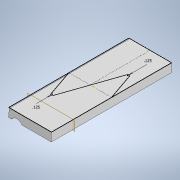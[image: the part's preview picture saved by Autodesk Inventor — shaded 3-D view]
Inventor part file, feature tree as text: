
AUTODESK INVENTOR PART (.ipt)
format: ipt  version: 2021.2 (Build 252289000, 289)  size: 352,768 bytes
history: native  units: in
note: dims shown in document units (in); Inventor stores cm internally (conversion verified against a paired STEP export)
features: sketch x4, extrude x2, hole x1, pattern_linear x1, plane x1, mirror x1
ambient origin geometry x8: Origin, YZ Plane, XZ Plane, XY Plane, X Axis, Y Axis, Z Axis, Center Point
bodies: Solid1 (feature_tree)
feature tree (10):
  extrude  "Extrusion1"  Depth=4.0in
  hole  "Hole2"  [1 undecoded]
  pattern_linear  "Rectangular Pattern1"  Spacing1=0.45in  [1 undecoded]
  extrude  "ExtrusionForText"  Depth=3.1496in
  plane  "Work Plane1"
  mirror  "MirrorHoles"
  sketch  "SketchForSplittingPart"  dims[d5=0.765in]
  sketch  "Sketch2"  dims[d0=6.0in d1=4.0in]
  sketch  "Sketch3"  dims[d2=0.8189in d4=1.135in]
  sketch  "SketchForText"  dims[d6=11.25in d7=0.0in d8=0.45in d16=0.13in d17=0.6in d18=0.563in d19=0.155in d20=0.5635in d21=0.625in d22=0.8108in d23=3.1496in d25=0.25in d26=0.05in d27=0.0in d30=0.125in d31=0.125in d32=-2.0in]
note: 2 required parameter values undecoded (feature->parameter linkage not recoverable at this tier; creation-order binding heuristic only, values carry confidence <= 0.55)
